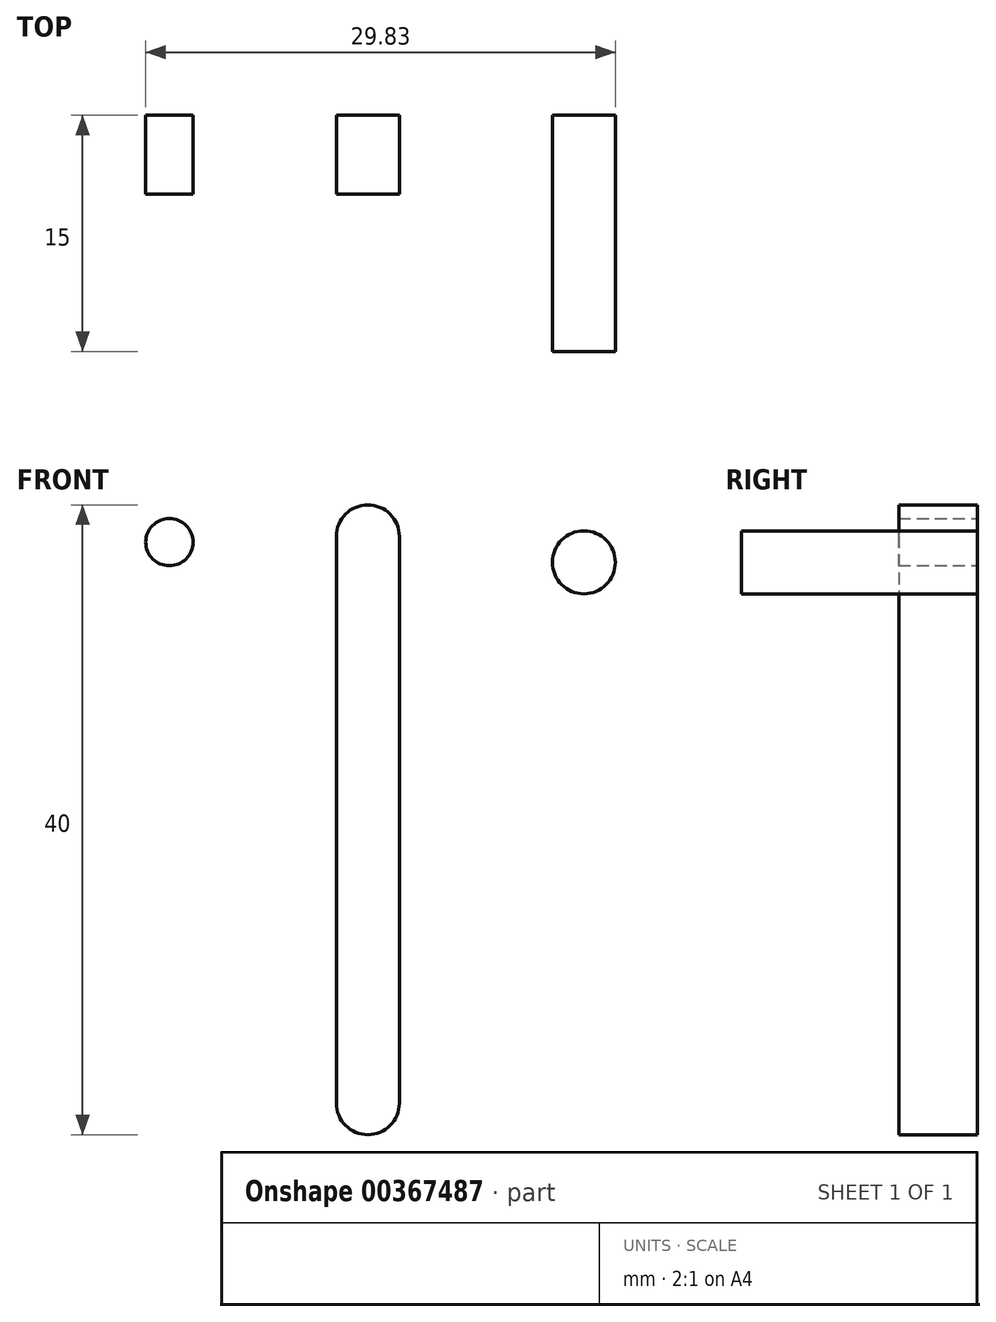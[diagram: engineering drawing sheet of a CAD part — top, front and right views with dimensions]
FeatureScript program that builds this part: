
annotation { "Feature Type Name" : "Feature", "Feature Type Description" : "" }
export const myFeature = defineFeature(function(context is Context, id is Id, definition is map)
    precondition{}
    {
        {
            var Q0;
            Q0=qCreatedBy(makeId("Front.planeOp"),FACE);
            var sketch = newSketch(context, id + "F0", { "sketchPlane" : qUnion([Q0])});
            skLineSegment(sketch, "E0.bottom", {"start": v(0, 20) * mm, "end": v(0, 20) * mm});
            skLineSegment(sketch, "E0.top", {"start": v(0, -20) * mm, "end": v(0, -20) * mm});
            skLineSegment(sketch, "E0.left", {"start": v(2, 18) * mm, "end": v(2, -18) * mm});
            skLineSegment(sketch, "E0.right", {"start": v(-2, 18) * mm, "end": v(-2, -18) * mm});
            skPoint(sketch, "E0.middle", {"position": v(0, 0) * mm});
            skPoint(sketch, "E1.visualSharp", {"position": v(-2, 20) * mm});
            skArc(sketch, "E1.filletArc", {"start": v(0, 20) * mm, "mid": v(-1.41, 19.41) * mm, "end": v(-2, 18) * mm});
            skPoint(sketch, "E2.visualSharp", {"position": v(2, 20) * mm});
            skArc(sketch, "E2.filletArc", {"start": v(2, 18) * mm, "mid": v(1.41, 19.41) * mm, "end": v(0, 20) * mm});
            skPoint(sketch, "E3.visualSharp", {"position": v(-2, -20) * mm});
            skArc(sketch, "E3.filletArc", {"start": v(-2, -18) * mm, "mid": v(-1.41, -19.41) * mm, "end": v(0, -20) * mm});
            skPoint(sketch, "E4.visualSharp", {"position": v(2, -20) * mm});
            skArc(sketch, "E4.filletArc", {"start": v(0, -20) * mm, "mid": v(1.41, -19.41) * mm, "end": v(2, -18) * mm});
            skSolve(sketch);
        }
        {
            var Q0;
            Q0=qCreatedBy(makeId("Front.planeOp"),FACE);
            var sketch = newSketch(context, id + "F1", { "sketchPlane" : qUnion([Q0])});
            skCircle(sketch, "E5", {"center": v(-12.6, 17.64) * mm, "radius": 1.5 * mm});
            skSolve(sketch);
        }
        {
            var Q0;
            Q0=qCreatedBy(makeId("Front.planeOp"),FACE);
            var sketch = newSketch(context, id + "F2", { "sketchPlane" : qUnion([Q0])});
            skCircle(sketch, "E6", {"center": v(13.72, 16.36) * mm, "radius": 2 * mm});
            skSolve(sketch);
        }
        {
            var Q0;
            Q0=makeQuery(id+"F2.imprint","IMPRINT",FACE,{"disambiguationData":[TD([[makeQuery(id+"F2.imprint","IMPRINT",EDGE,{"derivedFrom":sQuery(id+"F2.wireOp",EDGE,"E6")}),1.0]])]});
            extrude(context, id + "F3", {"entities" : qUnion([Q0]), "depth" : 15 * mm});
        }
        {
            var Q0;
            Q0=makeQuery(id+"F1.imprint","IMPRINT",FACE,{"disambiguationData":[TD([[makeQuery(id+"F1.imprint","IMPRINT",EDGE,{"derivedFrom":sQuery(id+"F1.wireOp",EDGE,"E5")}),1.0]])]});
            extrude(context, id + "F4", {"entities" : qUnion([Q0]), "depth" : 5 * mm});
        }
        {
            var Q0;
            Q0=makeQuery(id+"F0.imprint","IMPRINT",FACE,{"disambiguationData":[TD([[makeQuery(id+"F0.imprint","IMPRINT",EDGE,{"derivedFrom":sQuery(id+"F0.wireOp",EDGE,"E0.left")}),-1.0]])]});
            extrude(context, id + "F5", {"entities" : qUnion([Q0]), "depth" : 5 * mm});
        }
    });
